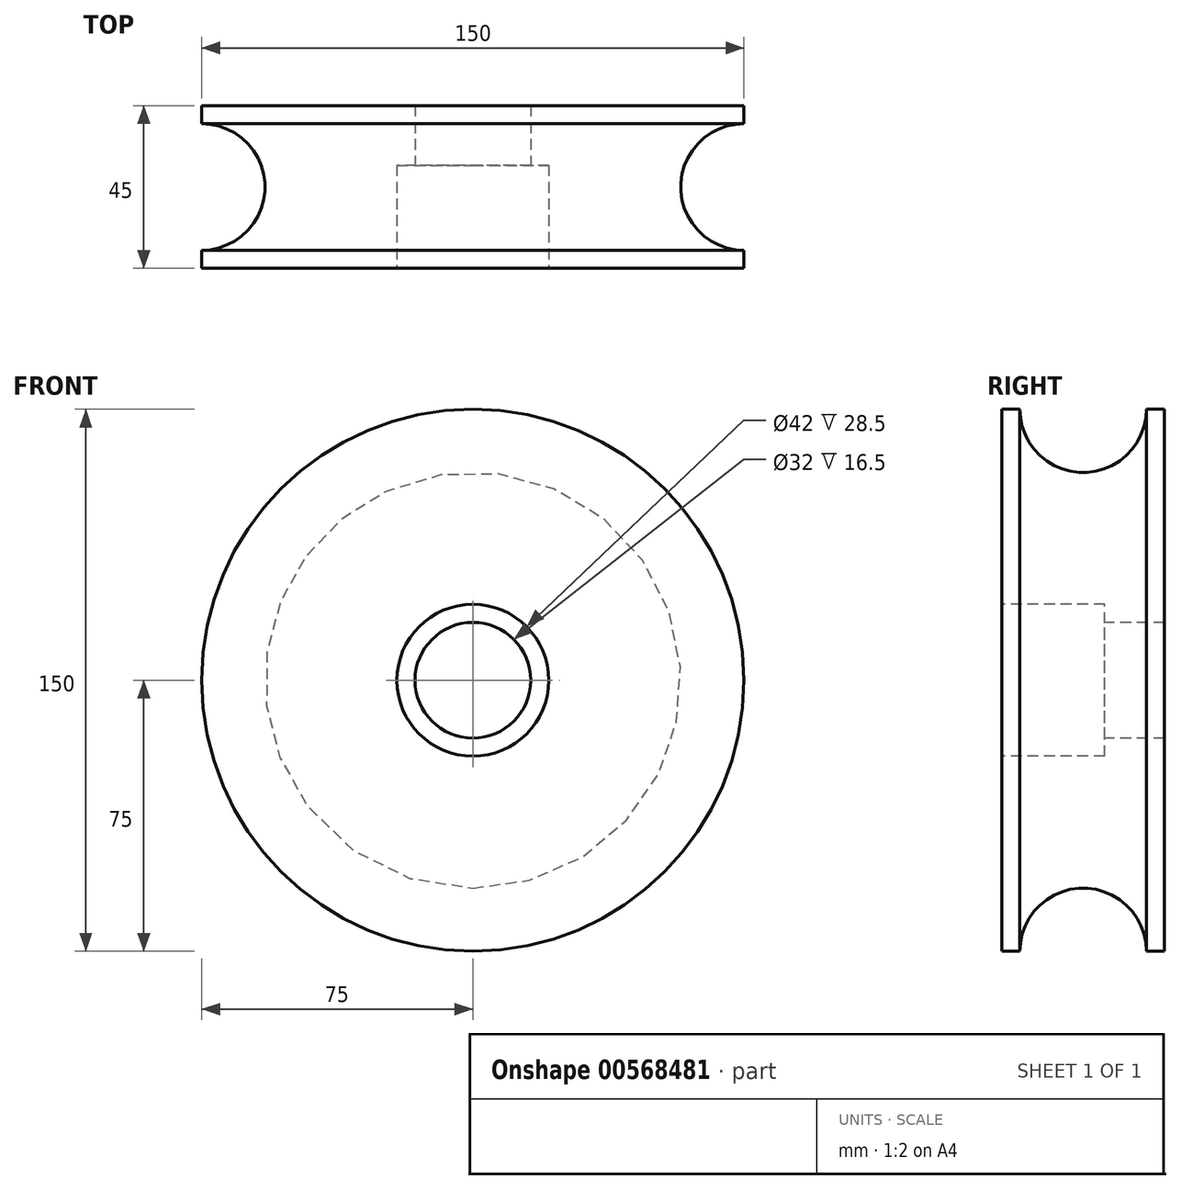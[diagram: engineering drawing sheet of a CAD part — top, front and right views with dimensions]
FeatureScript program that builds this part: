
annotation { "Feature Type Name" : "Feature", "Feature Type Description" : "" }
export const myFeature = defineFeature(function(context is Context, id is Id, definition is map)
    precondition{}
    {
        {
            var Q0;
            Q0=qCreatedBy(makeId("Front.planeOp"),FACE);
            var sketch = newSketch(context, id + "F0", { "sketchPlane" : qUnion([Q0])});
            skCircle(sketch, "E0", {"center": v(0, 0) * mm, "radius": 75 * mm});
            skSolve(sketch);
        }
        {
            var Q0;
            Q0=makeQuery(id+"F0.imprint","IMPRINT",FACE,{"disambiguationData":[TD([[makeQuery(id+"F0.imprint","IMPRINT",EDGE,{"derivedFrom":sQuery(id+"F0.wireOp",EDGE,"E0")}),1.0]])]});
            extrude(context, id + "F1", {"entities" : qUnion([Q0]), "endBound" : BoundingType.SYMMETRIC, "depth" : 45 * mm, "offsetDistance" : 25 * mm});
        }
        {
            var Q0;
            Q0=qCreatedBy(makeId("Top.planeOp"),FACE);
            var sketch = newSketch(context, id + "F2", { "sketchPlane" : qUnion([Q0])});
            skCircle(sketch, "E1", {"center": v(-75, 0) * mm, "radius": 17.5 * mm});
            skPoint(sketch, "E2", {"position": v(-57.5, 0) * mm});
            skSolve(sketch);
        }
        {
            var Q0;
            Q0=qCreatedBy(makeId("Top.planeOp"),FACE);
            var sketch = newSketch(context, id + "F3", { "sketchPlane" : qUnion([Q0])});
            skLineSegment(sketch, "E3", {"start": v(0, 71.9) * mm, "end": v(0, -63.09) * mm});
            skSolve(sketch);
        }
        {
            var Q0;
            Q0 = qSketchRegion(id + "F2", true);
            var Q1;
            Q1=sQuery(id+"F3.wireOp",EDGE,"E3");
            revolve(context, id + "F4", {"operationType" : NewBodyOperationType.REMOVE, "entities" : qUnion([Q0]), "axis" : qUnion([Q1]), "revolveType" : RevolveType.FULL, "oppositeDirection" : true});
        }
        {
            var Q0;
            Q0=makeQuery(id+"F1.opExtrude","CAP_FACE",FACE,{"disambiguationData":[OSD([sQuery(id+"F0.wireOp",EDGE,"E0")])],"isStart":false});
            var sketch = newSketch(context, id + "F5", { "sketchPlane" : qUnion([Q0])});
            skPoint(sketch, "E4", {"position": v(0, 0) * mm});
            skCircle(sketch, "E5", {"center": v(0, 0) * mm, "radius": 21 * mm});
            skSolve(sketch);
        }
        {
            var Q0;
            Q0=makeQuery(id+"F5.imprint","IMPRINT",FACE,{"disambiguationData":[TD([[makeQuery(id+"F5.imprint","IMPRINT",EDGE,{"derivedFrom":sQuery(id+"F5.wireOp",EDGE,"E5")}),1.0]])]});
            extrude(context, id + "F6", {"entities" : qUnion([Q0]), "operationType" : NewBodyOperationType.REMOVE, "oppositeDirection" : true, "depth" : 28.5 * mm, "offsetDistance" : 25 * mm});
        }
        {
            var Q0;
            Q0=makeQuery(id+"F1.opExtrude","CAP_FACE",FACE,{"disambiguationData":[OSD([sQuery(id+"F0.wireOp",EDGE,"E0")])],"isStart":false});
            var sketch = newSketch(context, id + "F7", { "sketchPlane" : qUnion([Q0])});
            skCircle(sketch, "E6", {"center": v(0, 0) * mm, "radius": 16 * mm});
            skSolve(sketch);
        }
        {
            var Q0;
            Q0=makeQuery(id+"F7.imprint","IMPRINT",FACE,{"disambiguationData":[TD([[makeQuery(id+"F7.imprint","IMPRINT",EDGE,{"derivedFrom":sQuery(id+"F7.wireOp",EDGE,"E6")}),1.0]])]});
            var Q1;
            Q1=makeQuery(id+"F1.opExtrude","CAP_FACE",FACE,{"disambiguationData":[OSD([sQuery(id+"F0.wireOp",EDGE,"E0")])],"isStart":true});
            extrude(context, id + "F8", {"entities" : qUnion([Q0, Q1]), "operationType" : NewBodyOperationType.REMOVE, "endBound" : BoundingType.THROUGH_ALL, "oppositeDirection" : true, "depth" : 25 * mm, "offsetDistance" : 25 * mm});
        }
    });
